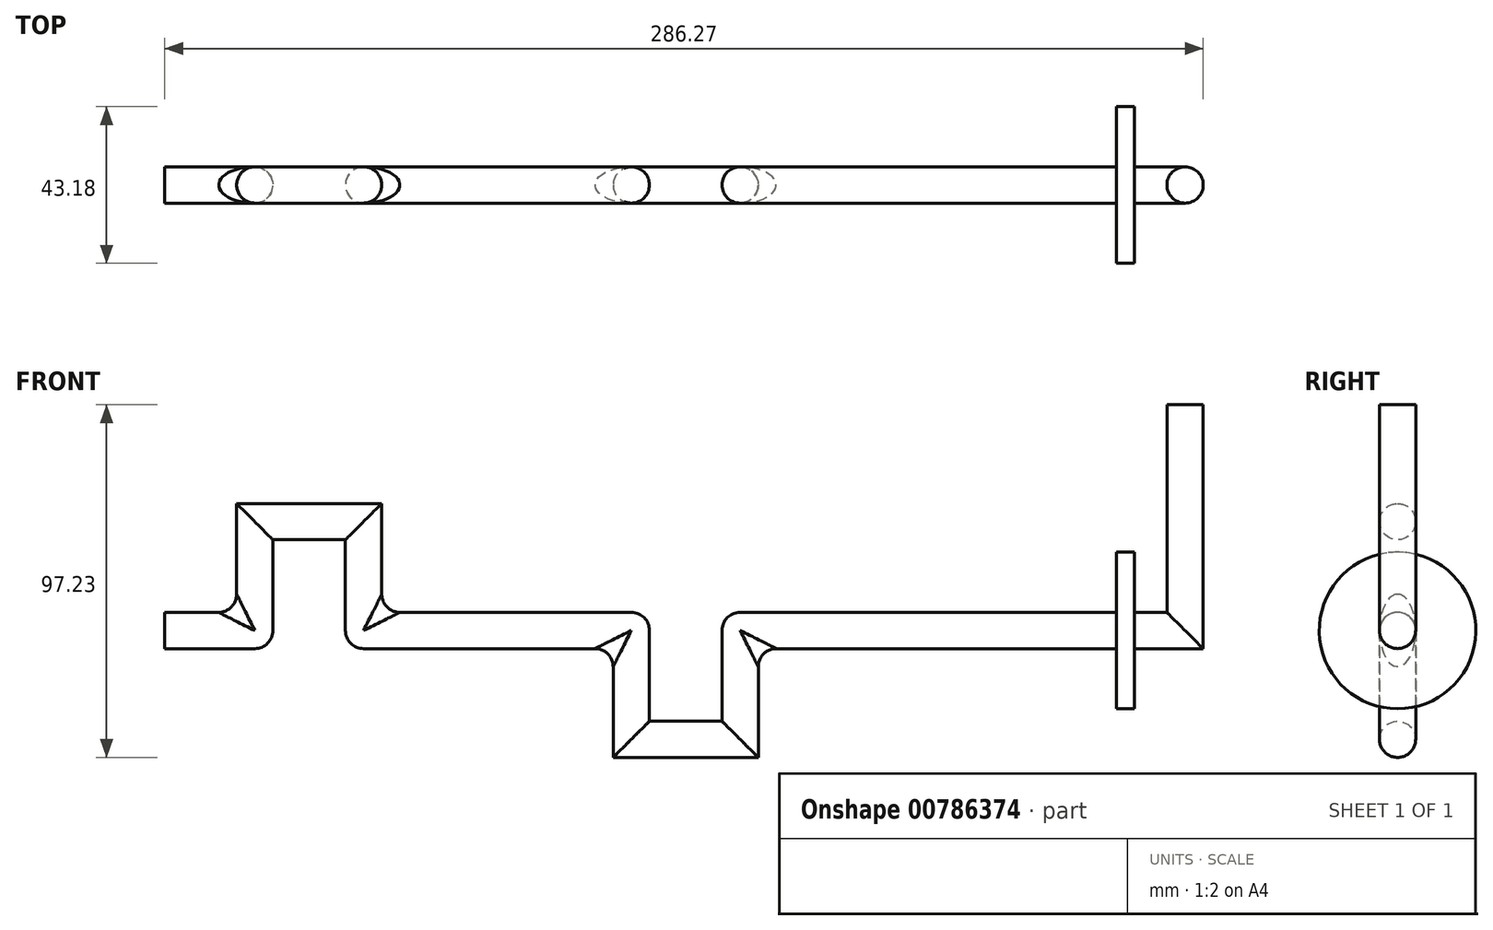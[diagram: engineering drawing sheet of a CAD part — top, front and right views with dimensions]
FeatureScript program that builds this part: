
annotation { "Feature Type Name" : "Feature", "Feature Type Description" : "" }
export const myFeature = defineFeature(function(context is Context, id is Id, definition is map)
    precondition{}
    {
        {
            var Q0;
            Q0=qCreatedBy(makeId("Front.planeOp"),FACE);
            var sketch = newSketch(context, id + "F0", { "sketchPlane" : qUnion([Q0])});
            skLineSegment(sketch, "E0", {"start": v(36.06, 0) * mm, "end": v(-37.74, 0) * mm});
            skLineSegment(sketch, "E1", {"start": v(-37.74, 0) * mm, "end": v(-37.74, 30) * mm});
            skLineSegment(sketch, "E2", {"start": v(-37.74, 30) * mm, "end": v(-67.74, 30) * mm});
            skLineSegment(sketch, "E3", {"start": v(-67.74, 30) * mm, "end": v(-67.74, 0) * mm});
            skLineSegment(sketch, "E4", {"start": v(-67.74, 0) * mm, "end": v(-92.56, 0) * mm});
            skLineSegment(sketch, "E5", {"start": v(36.06, -30) * mm, "end": v(36.06, 0) * mm});
            skLineSegment(sketch, "E6", {"start": v(66.06, 0) * mm, "end": v(66.06, 0) * mm});
            skLineSegment(sketch, "E7", {"start": v(66.06, -30) * mm, "end": v(36.06, -30) * mm});
            skLineSegment(sketch, "E8", {"start": v(66.06, 0) * mm, "end": v(66.06, -30) * mm});
            skLineSegment(sketch, "E9", {"start": v(106.69, 0) * mm, "end": v(66.06, 0) * mm});
            skLineSegment(sketch, "E10", {"start": v(106.69, 0) * mm, "end": v(169.74, 0) * mm});
            skSolve(sketch);
        }
        {
            var Q0;
            Q0=qCreatedBy(makeId("Right.planeOp"),FACE);
            var Q1;
            Q1=sQuery(id+"F0.wireOp",VERTEX,"E10.end");
            cPlane(context, id + "F1", {"entities" : qUnion([Q0, Q1]), "cplaneType" : CPlaneType.PLANE_POINT, "offset" : 25 * mm, "width" : 150 * mm, "height" : 150 * mm});
        }
        {
            var Q0;
            Q0=qCreatedBy(id+"F1.planeOp",FACE);
            var sketch = newSketch(context, id + "F2", { "sketchPlane" : qUnion([Q0])});
            skCircle(sketch, "E11", {"center": v(0, 0) * mm, "radius": 5 * mm});
            skCircle(sketch, "E12.0", {"center": v(0, 0) * mm, "radius": 21.59 * mm});
            skSolve(sketch);
        }
        {
            var Q0;
            Q0=makeQuery(id+"F2.imprint","IMPRINT",FACE,{"disambiguationData":[TD([[makeQuery(id+"F2.imprint","IMPRINT",EDGE,{"derivedFrom":sQuery(id+"F2.wireOp",EDGE,"E11")}),1.0]])]});
            var Q1;
            Q1=sQuery(id+"F0.wireOp",EDGE,"E10");
            var Q2;
            Q2=sQuery(id+"F0.wireOp",EDGE,"E9");
            var Q3;
            Q3=sQuery(id+"F0.wireOp",EDGE,"E8");
            var Q4;
            Q4=sQuery(id+"F0.wireOp",EDGE,"E7");
            var Q5;
            Q5=sQuery(id+"F0.wireOp",EDGE,"E5");
            var Q6;
            Q6=sQuery(id+"F0.wireOp",EDGE,"E0");
            var Q7;
            Q7=sQuery(id+"F0.wireOp",EDGE,"E1");
            var Q8;
            Q8=sQuery(id+"F0.wireOp",EDGE,"E2");
            var Q9;
            Q9=sQuery(id+"F0.wireOp",EDGE,"E3");
            var Q10;
            Q10=sQuery(id+"F0.wireOp",EDGE,"E4");
            sweep(context, id + "F3", {"profiles" : qUnion([Q0]), "path" : qUnion([Q1, Q2, Q3, Q4, Q5, Q6, Q7, Q8, Q9, Q10])});
        }
        {
            var Q0;
            Q0=makeQuery(id+"F3.opSweep","MID_CAP_EDGE",EDGE,{"disambiguationData":[OSD([sQuery(id+"F0.wireOp",VERTEX,"E8.start"),sQuery(id+"F2.wireOp",EDGE,"E11")])],"capPos":2.0});
            var Q1;
            Q1=makeQuery(id+"F3.opSweep","MID_CAP_EDGE",EDGE,{"disambiguationData":[OSD([sQuery(id+"F0.wireOp",VERTEX,"E0.start"),sQuery(id+"F2.wireOp",EDGE,"E11")])],"capPos":5.0});
            var Q2;
            Q2=makeQuery(id+"F3.opSweep","MID_CAP_EDGE",EDGE,{"disambiguationData":[OSD([sQuery(id+"F0.wireOp",VERTEX,"E1.start"),sQuery(id+"F2.wireOp",EDGE,"E11")])],"capPos":6.0});
            var Q3;
            Q3=makeQuery(id+"F3.opSweep","MID_CAP_EDGE",EDGE,{"disambiguationData":[OSD([sQuery(id+"F0.wireOp",VERTEX,"E4.start"),sQuery(id+"F2.wireOp",EDGE,"E11")])],"capPos":9.0});
            fillet(context, id + "F4", {"entities" : qUnion([Q0, Q1, Q2, Q3]), "radius" : 5 * mm, "tangentPropagation" : true, "allowEdgeOverflow" : false});
        }
        {
            var Q0;
            Q0=makeQuery(id+"F2.imprint","IMPRINT",FACE,{"disambiguationData":[TD([[makeQuery(id+"F2.imprint","IMPRINT",EDGE,{"derivedFrom":sQuery(id+"F2.wireOp",EDGE,"E11")}),-1.0]])]});
            var Q1;
            Q1=makeQuery(id+"F2.imprint","IMPRINT",FACE,{"disambiguationData":[TD([[makeQuery(id+"F2.imprint","IMPRINT",EDGE,{"derivedFrom":sQuery(id+"F2.wireOp",EDGE,"E11")}),1.0]])]});
            extrude(context, id + "F5", {"entities" : qUnion([Q0, Q1]), "operationType" : NewBodyOperationType.ADD, "depth" : 5 * mm, "offsetDistance" : 25 * mm});
        }
        {
            var Q0;
            Q0=qCreatedBy(makeId("Front.planeOp"),FACE);
            var sketch = newSketch(context, id + "F6", { "sketchPlane" : qUnion([Q0])});
            skLineSegment(sketch, "E13", {"start": v(174.9, 0) * mm, "end": v(188.71, 0) * mm});
            skLineSegment(sketch, "E14", {"start": v(188.71, 0) * mm, "end": v(188.71, 67.4) * mm});
            skSolve(sketch);
        }
        {
            var Q0;
            Q0=makeQuery(id+"F2.imprint","IMPRINT",FACE,{"disambiguationData":[TD([[makeQuery(id+"F2.imprint","IMPRINT",EDGE,{"derivedFrom":sQuery(id+"F2.wireOp",EDGE,"E11")}),1.0]])]});
            var Q1;
            Q1=sQuery(id+"F6.wireOp",EDGE,"E13");
            var Q2;
            Q2=sQuery(id+"F6.wireOp",EDGE,"E14");
            sweep(context, id + "F7", {"operationType" : NewBodyOperationType.ADD, "profiles" : qUnion([Q0]), "path" : qUnion([Q1, Q2])});
        }
    });
